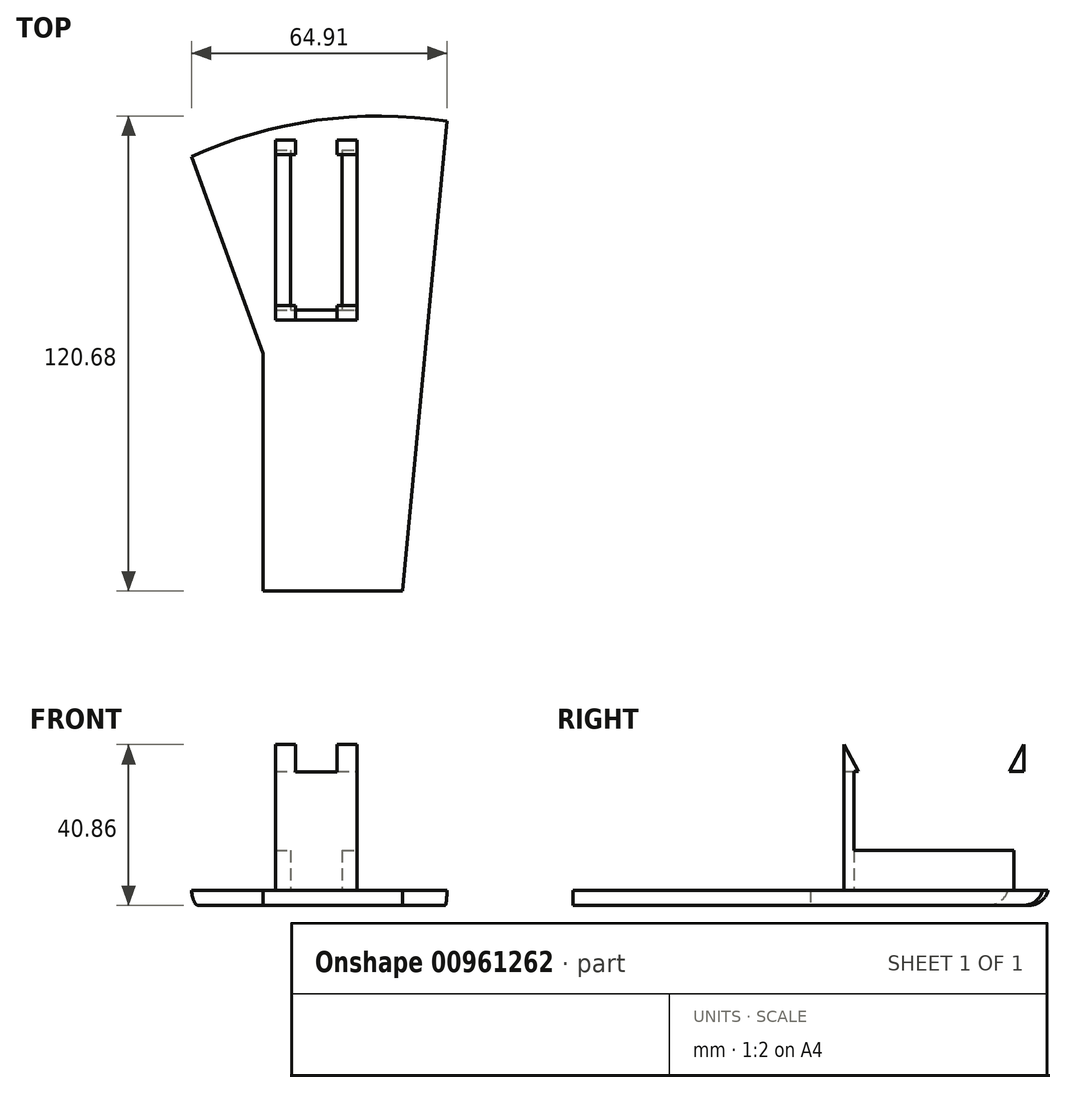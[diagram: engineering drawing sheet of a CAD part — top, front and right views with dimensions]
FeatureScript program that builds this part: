
annotation { "Feature Type Name" : "Feature", "Feature Type Description" : "" }
export const myFeature = defineFeature(function(context is Context, id is Id, definition is map)
    precondition{}
    {
        {
            var Q0;
            Q0=qCreatedBy(makeId("Top.planeOp"),FACE);
            var sketch = newSketch(context, id + "F0", { "sketchPlane" : qUnion([Q0])});
            skLineSegment(sketch, "E0", {"start": v(-32.56, 17.14) * mm, "end": v(32.35, 26.1) * mm});
            skLineSegment(sketch, "E1", {"start": v(32.35, 26.1) * mm, "end": v(21.05, -93.25) * mm});
            skLineSegment(sketch, "E2", {"start": v(21.05, -93.25) * mm, "end": v(-14.33, -93.25) * mm});
            skLineSegment(sketch, "E3", {"start": v(-14.33, -93.25) * mm, "end": v(-14.33, -32.95) * mm});
            skLineSegment(sketch, "E4", {"start": v(-14.33, -32.95) * mm, "end": v(-32.56, 17.14) * mm});
            skArc(sketch, "E5", {"start": v(32.35, 26.1) * mm, "mid": v(-0.76, 26.35) * mm, "end": v(-32.56, 17.14) * mm});
            skSolve(sketch);
        }
        {
            var Q0;
            Q0=makeQuery(id+"F0.imprint","IMPRINT",FACE,{"disambiguationData":[TD([[makeQuery(id+"F0.imprint","IMPRINT",EDGE,{"derivedFrom":sQuery(id+"F0.wireOp",EDGE,"E0")}),1.0]])]});
            var Q1;
            Q1=makeQuery(id+"F0.imprint","IMPRINT",FACE,{"disambiguationData":[TD([[makeQuery(id+"F0.imprint","IMPRINT",EDGE,{"derivedFrom":sQuery(id+"F0.wireOp",EDGE,"E0")}),-1.0]])]});
            extrude(context, id + "F1", {"entities" : qUnion([Q0, Q1]), "depth" : 3.8 * mm, "offsetDistance" : 25.4 * mm});
        }
        {
            var Q0;
            Q0=makeQuery(id+"F1.opExtrude","CAP_FACE",FACE,{"disambiguationData":[OSD([sQuery(id+"F0.wireOp",EDGE,"E1"),sQuery(id+"F0.wireOp",EDGE,"E2"),sQuery(id+"F0.wireOp",EDGE,"E3"),sQuery(id+"F0.wireOp",EDGE,"E4"),sQuery(id+"F0.wireOp",EDGE,"E5")])],"isStart":false});
            var sketch = newSketch(context, id + "F2", { "sketchPlane" : qUnion([Q0])});
            skLineSegment(sketch, "E6.bottom", {"start": v(-11.22, 18.8) * mm, "end": v(9.5, 18.8) * mm});
            skLineSegment(sketch, "E6.top", {"start": v(-11.22, -21.85) * mm, "end": v(9.5, -21.85) * mm});
            skLineSegment(sketch, "E7", {"start": v(-11.22, 18.8) * mm, "end": v(-11.22, -21.85) * mm});
            skPoint(sketch, "E7.endSnap0", {"position": v(-9.94, -21.85) * mm});
            skLineSegment(sketch, "E8", {"start": v(9.5, -21.85) * mm, "end": v(9.5, 18.8) * mm});
            skPoint(sketch, "E9.orphan", {"position": v(71.14, -21.85) * mm});
            skPoint(sketch, "E10.orphan", {"position": v(-91.02, -21.85) * mm});
            skLineSegment(sketch, "E11.top", {"start": v(-11.22, 21.33) * mm, "end": v(9.5, 21.33) * mm});
            skLineSegment(sketch, "E11.left", {"start": v(-11.22, 18.8) * mm, "end": v(-11.22, 21.33) * mm});
            skLineSegment(sketch, "E11.right", {"start": v(9.5, 18.8) * mm, "end": v(9.5, 21.33) * mm});
            skLineSegment(sketch, "E12.top", {"start": v(-11.22, -24.39) * mm, "end": v(9.5, -24.39) * mm});
            skLineSegment(sketch, "E12.left", {"start": v(-11.22, -21.85) * mm, "end": v(-11.22, -24.39) * mm});
            skLineSegment(sketch, "E12.right", {"start": v(9.5, -21.85) * mm, "end": v(9.5, -24.39) * mm});
            skSolve(sketch);
        }
        {
            var Q0;
            Q0=makeQuery(id+"F1.opExtrude","CAP_EDGE",EDGE,{"disambiguationData":[OSD([sQuery(id+"F0.wireOp",EDGE,"E5")])],"isStart":true});
            fillet(context, id + "F3", {"entities" : qUnion([Q0]), "radius" : 5.08 * mm, "tangentPropagation" : true, "allowEdgeOverflow" : false});
        }
        {
            var Q0;
            Q0=makeQuery(id+"F2.imprint","IMPRINT",FACE,{"disambiguationData":[TD([[makeQuery(id+"F2.imprint","IMPRINT",EDGE,{"derivedFrom":sQuery(id+"F2.wireOp",EDGE,"E6.bottom")}),1.0]])]});
            var Q1;
            Q1=makeQuery(id+"F2.imprint","IMPRINT",FACE,{"disambiguationData":[TD([[makeQuery(id+"F2.imprint","IMPRINT",EDGE,{"derivedFrom":sQuery(id+"F2.wireOp",EDGE,"E6.top")}),-1.0]])]});
            extrude(context, id + "F4", {"entities" : qUnion([Q0, Q1]), "operationType" : NewBodyOperationType.ADD, "depth" : 30.23 * mm, "offsetDistance" : 25.4 * mm});
        }
        {
            var Q0;
            Q0=makeQuery(id+"F1.opExtrude","CAP_FACE",FACE,{"disambiguationData":[OSD([sQuery(id+"F0.wireOp",EDGE,"E1"),sQuery(id+"F0.wireOp",EDGE,"E2"),sQuery(id+"F0.wireOp",EDGE,"E3"),sQuery(id+"F0.wireOp",EDGE,"E4"),sQuery(id+"F0.wireOp",EDGE,"E5")])],"isStart":false});
            var sketch = newSketch(context, id + "F5", { "sketchPlane" : qUnion([Q0])});
            skSolve(sketch);
        }
        {
            var Q0;
            {var subQ4=sQuery(id+"F0.wireOp",EDGE,"E1");Q0=makeQuery(id+"F5.imprint","IMPRINT",FACE,{"disambiguationData":[TD([[makeQuery(id+"F5.imprint","IMPRINT",EDGE,{"derivedFrom":makeQuery(id+"F1.opExtrude","CAP_EDGE",EDGE,{"disambiguationData":[OSD([subQ4])],"isStart":false})}),-1.0]])]});}
            var sketch = newSketch(context, id + "F6", { "sketchPlane" : qUnion([Q0])});
            skLineSegment(sketch, "E13.bottom", {"start": v(-7.41, 18.8) * mm, "end": v(5.68, 18.8) * mm});
            skLineSegment(sketch, "E13.top", {"start": v(-7.41, -21.85) * mm, "end": v(5.68, -21.85) * mm});
            skLineSegment(sketch, "E13.left", {"start": v(-7.41, 18.8) * mm, "end": v(-7.41, -21.85) * mm});
            skLineSegment(sketch, "E13.right", {"start": v(5.68, 18.8) * mm, "end": v(5.68, -21.85) * mm});
            skLineSegment(sketch, "E14.bottom", {"start": v(-11.22, 18.8) * mm, "end": v(9.5, 18.8) * mm});
            skLineSegment(sketch, "E14.top", {"start": v(-11.22, -21.85) * mm, "end": v(9.5, -21.85) * mm});
            skLineSegment(sketch, "E14.left", {"start": v(-11.22, 18.8) * mm, "end": v(-11.22, -21.85) * mm});
            skLineSegment(sketch, "E14.right", {"start": v(9.5, 18.8) * mm, "end": v(9.5, -21.85) * mm});
            skSolve(sketch);
        }
        {
            var Q0;
            Q0=makeQuery(id+"F4.opExtrude","SWEPT_FACE",FACE,{"disambiguationData":[OSD([sQuery(id+"F2.wireOp",EDGE,"E12.right")])]});
            var sketch = newSketch(context, id + "F7", { "sketchPlane" : qUnion([Q0])});
            skLineSegment(sketch, "E15", {"start": v(-24.39, 34.04) * mm, "end": v(-24.39, 40.86) * mm});
            skLineSegment(sketch, "E16", {"start": v(-24.39, 40.86) * mm, "end": v(-20.66, 34.04) * mm});
            skLineSegment(sketch, "E17", {"start": v(-20.66, 34.04) * mm, "end": v(-24.39, 34.04) * mm});
            skLineSegment(sketch, "E18", {"start": v(21.33, 34.04) * mm, "end": v(21.33, 40.86) * mm});
            skLineSegment(sketch, "E19", {"start": v(21.33, 40.86) * mm, "end": v(17.6, 34.04) * mm});
            skLineSegment(sketch, "E20", {"start": v(17.6, 34.04) * mm, "end": v(21.33, 34.04) * mm});
            skSolve(sketch);
        }
        {
            var Q0;
            {var subQ0=sQuery(id+"F7.wireOp",EDGE,"E15");Q0=makeQuery(id+"F7.imprint","IMPRINT",FACE,{"disambiguationData":[TD([[makeQuery(id+"F7.imprint","IMPRINT",EDGE,{"derivedFrom":subQ0}),-1.0]])]});}
            var Q1;
            Q1=makeQuery(id+"F7.imprint","IMPRINT",FACE,{"disambiguationData":[TD([[makeQuery(id+"F7.imprint","IMPRINT",EDGE,{"derivedFrom":sQuery(id+"F7.wireOp",EDGE,"E18")}),1.0]])]});
            extrude(context, id + "F8", {"entities" : qUnion([Q0, Q1]), "operationType" : NewBodyOperationType.ADD, "oppositeDirection" : true, "depth" : 20.71 * mm, "offsetDistance" : 25.4 * mm});
        }
        {
            var Q0;
            Q0=makeQuery(id+"F8.boolean.opBoolean","MERGE",FACE,{"derivedFrom":[makeQuery(id+"F4.opExtrude","SWEPT_FACE",FACE,{"disambiguationData":[OSD([sQuery(id+"F2.wireOp",EDGE,"E12.top")])]}),makeQuery(id+"F8.opExtrude","SWEPT_FACE",FACE,{"disambiguationData":[OSD([sQuery(id+"F7.wireOp",EDGE,"E15")])]})]});
            var sketch = newSketch(context, id + "F9", { "sketchPlane" : qUnion([Q0])});
            skLineSegment(sketch, "E21.bottom", {"start": v(-6.14, 40.86) * mm, "end": v(4.41, 40.86) * mm});
            skLineSegment(sketch, "E21.top", {"start": v(-6.14, 33.86) * mm, "end": v(4.41, 33.86) * mm});
            skLineSegment(sketch, "E21.left", {"start": v(-6.14, 40.86) * mm, "end": v(-6.14, 33.86) * mm});
            skLineSegment(sketch, "E21.right", {"start": v(4.41, 40.86) * mm, "end": v(4.41, 33.86) * mm});
            skSolve(sketch);
        }
        {
            var Q0;
            Q0=makeQuery(id+"F9.imprint","IMPRINT",FACE,{"disambiguationData":[TD([[makeQuery(id+"F9.imprint","IMPRINT",EDGE,{"derivedFrom":sQuery(id+"F9.wireOp",EDGE,"E21.bottom")}),-1.0]])]});
            extrude(context, id + "F10", {"entities" : qUnion([Q0]), "operationType" : NewBodyOperationType.REMOVE, "endBound" : BoundingType.THROUGH_ALL, "oppositeDirection" : true, "depth" : 25.4 * mm, "offsetDistance" : 25.4 * mm});
        }
        {
            var Q0;
            {var subQ0=sQuery(id+"F6.wireOp",EDGE,"E13.right");Q0=makeQuery(id+"F6.imprint","IMPRINT",FACE,{"disambiguationData":[TD([[makeQuery(id+"F6.imprint","IMPRINT",EDGE,{"derivedFrom":subQ0}),1.0]])]});}
            var Q1;
            {var subQ0=sQuery(id+"F6.wireOp",EDGE,"E13.left");Q1=makeQuery(id+"F6.imprint","IMPRINT",FACE,{"disambiguationData":[TD([[makeQuery(id+"F6.imprint","IMPRINT",EDGE,{"derivedFrom":subQ0}),-1.0]])]});}
            extrude(context, id + "F11", {"entities" : qUnion([Q0, Q1]), "operationType" : NewBodyOperationType.ADD, "depth" : 10.16 * mm, "offsetDistance" : 25.4 * mm});
        }
    });
